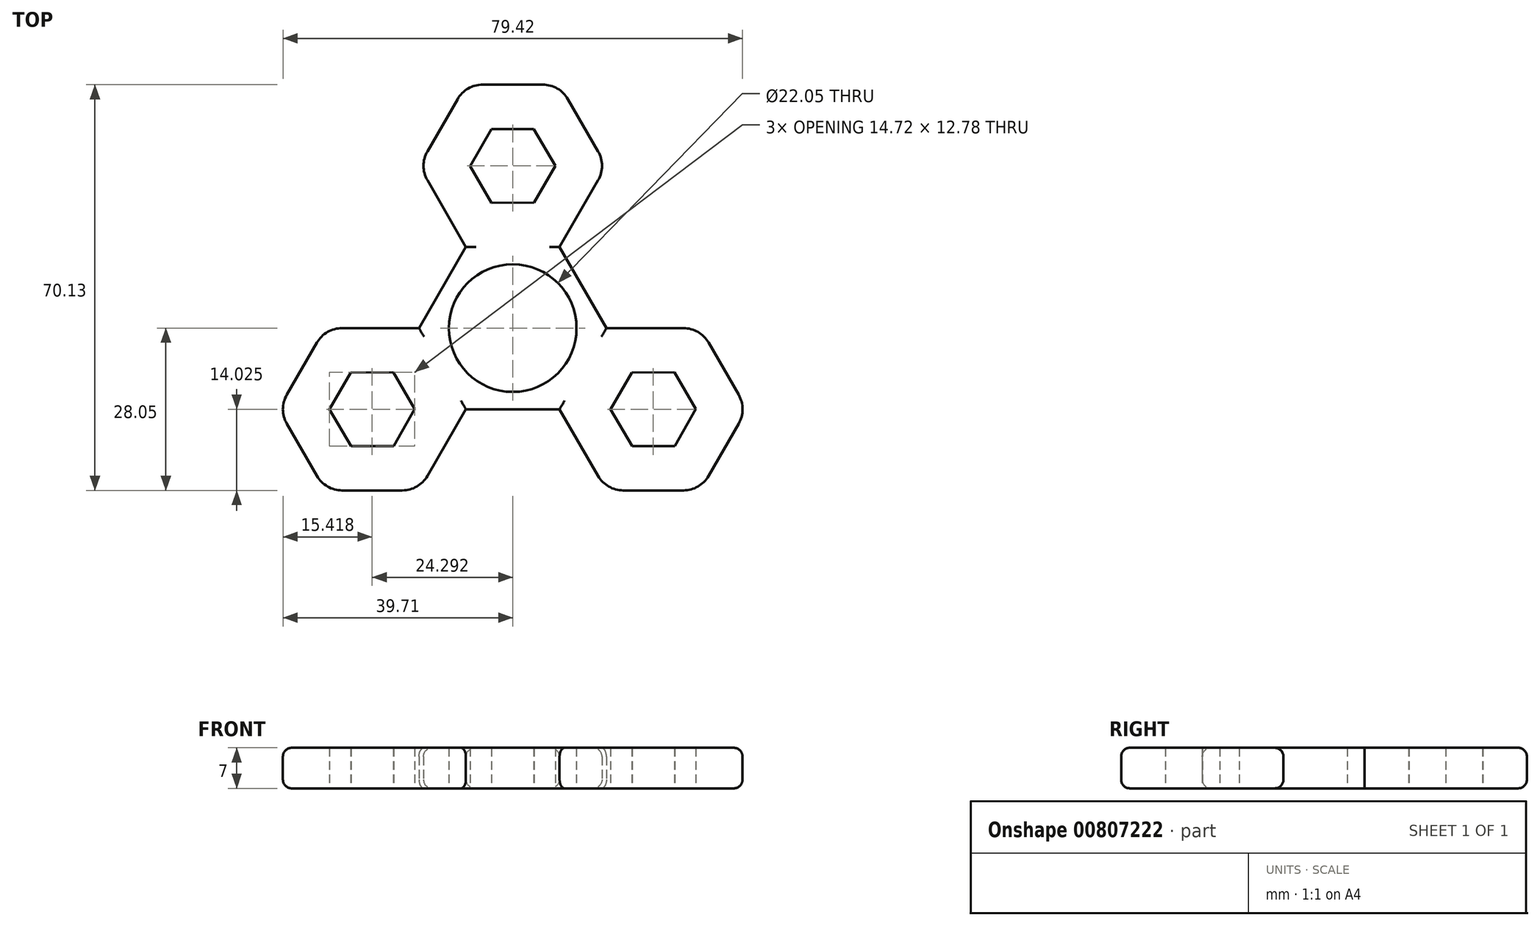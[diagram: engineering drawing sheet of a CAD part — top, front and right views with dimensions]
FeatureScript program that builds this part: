
annotation { "Feature Type Name" : "Feature", "Feature Type Description" : "" }
export const myFeature = defineFeature(function(context is Context, id is Id, definition is map)
    precondition{}
    {
        {
            var Q0;
            Q0=qCreatedBy(makeId("Top.planeOp"),FACE);
            var sketch = newSketch(context, id + "F0", { "sketchPlane" : qUnion([Q0])});
            skCircle(sketch, "E0", {"center": v(0, 0) * mm, "radius": 11.03 * mm});
            skCircle(sketch, "E1.cCircle", {"center": v(0, 0) * mm, "radius": 14.03 * mm, "construction": true});
            skLineSegment(sketch, "E1.1", {"start": v(8.1, -14.02) * mm, "end": v(-8.1, -14.03) * mm});
            skLineSegment(sketch, "E1.3", {"start": v(-16.2, 0) * mm, "end": v(-8.1, 14.03) * mm});
            skLineSegment(sketch, "E1.5", {"start": v(8.1, 14.02) * mm, "end": v(16.2, 0) * mm});
            skPoint(sketch, "E1.0.midPoint", {"position": v(12.15, -7.01) * mm});
            skCircle(sketch, "E2.cCircle", {"center": v(0, 28.05) * mm, "radius": 6.38 * mm, "construction": true});
            skLineSegment(sketch, "E2.0", {"start": v(7.36, 28.08) * mm, "end": v(3.7, 21.69) * mm});
            skLineSegment(sketch, "E2.1", {"start": v(3.7, 21.69) * mm, "end": v(-3.66, 21.66) * mm});
            skLineSegment(sketch, "E2.2", {"start": v(-3.66, 21.66) * mm, "end": v(-7.36, 28.02) * mm});
            skLineSegment(sketch, "E2.3", {"start": v(-7.36, 28.02) * mm, "end": v(-3.7, 34.41) * mm});
            skLineSegment(sketch, "E2.4", {"start": v(-3.7, 34.41) * mm, "end": v(3.66, 34.44) * mm});
            skLineSegment(sketch, "E2.5", {"start": v(3.66, 34.44) * mm, "end": v(7.36, 28.08) * mm});
            skPoint(sketch, "E2.0.midPoint", {"position": v(5.53, 24.88) * mm});
            skCircle(sketch, "E3.cCircle", {"center": v(0, 28.05) * mm, "radius": 14.03 * mm, "construction": true});
            skLineSegment(sketch, "E3.0", {"start": v(16.2, 28.05) * mm, "end": v(8.1, 14.02) * mm});
            skLineSegment(sketch, "E3.2", {"start": v(-8.1, 14.02) * mm, "end": v(-16.2, 28.05) * mm});
            skLineSegment(sketch, "E3.3", {"start": v(-16.2, 28.05) * mm, "end": v(-8.1, 42.07) * mm});
            skLineSegment(sketch, "E3.4", {"start": v(-8.1, 42.07) * mm, "end": v(8.1, 42.07) * mm});
            skLineSegment(sketch, "E3.5", {"start": v(8.1, 42.07) * mm, "end": v(16.2, 28.05) * mm});
            skPoint(sketch, "E3.0.midPoint", {"position": v(12.15, 21.04) * mm});
            skLineSegment(sketch, "E4.1.6", {"start": v(-16.2, -28.05) * mm, "end": v(-32.39, -28.05) * mm});
            skLineSegment(sketch, "E4.1.7", {"start": v(-32.39, -28.05) * mm, "end": v(-40.49, -14.02) * mm});
            skLineSegment(sketch, "E4.1.8", {"start": v(-40.49, -14.02) * mm, "end": v(-32.39, 0) * mm});
            skLineSegment(sketch, "E4.1.9", {"start": v(-32.39, 0) * mm, "end": v(-16.2, 0) * mm});
            skLineSegment(sketch, "E4.1.10", {"start": v(-8.1, -14.02) * mm, "end": v(-16.2, -28.05) * mm});
            skLineSegment(sketch, "E4.2.6", {"start": v(32.39, 0) * mm, "end": v(40.49, -14.02) * mm});
            skLineSegment(sketch, "E4.2.7", {"start": v(40.49, -14.02) * mm, "end": v(32.39, -28.05) * mm});
            skLineSegment(sketch, "E4.2.8", {"start": v(32.39, -28.05) * mm, "end": v(16.2, -28.05) * mm});
            skLineSegment(sketch, "E4.2.9", {"start": v(16.2, -28.05) * mm, "end": v(8.1, -14.02) * mm});
            skLineSegment(sketch, "E4.2.10", {"start": v(16.2, 0) * mm, "end": v(32.39, 0) * mm});
            skLineSegment(sketch, "E5.1.0", {"start": v(-27.95, -20.41) * mm, "end": v(-31.65, -14.05) * mm});
            skLineSegment(sketch, "E5.1.1", {"start": v(-31.65, -14.05) * mm, "end": v(-28, -7.66) * mm});
            skLineSegment(sketch, "E5.1.2", {"start": v(-28, -7.66) * mm, "end": v(-20.63, -7.64) * mm});
            skLineSegment(sketch, "E5.1.3", {"start": v(-20.63, -7.64) * mm, "end": v(-16.93, -14) * mm});
            skLineSegment(sketch, "E5.1.4", {"start": v(-16.93, -14) * mm, "end": v(-20.59, -20.39) * mm});
            skLineSegment(sketch, "E5.1.5", {"start": v(-20.59, -20.39) * mm, "end": v(-27.95, -20.41) * mm});
            skLineSegment(sketch, "E5.2.0", {"start": v(31.65, -14) * mm, "end": v(28, -20.39) * mm});
            skLineSegment(sketch, "E5.2.1", {"start": v(28, -20.39) * mm, "end": v(20.63, -20.41) * mm});
            skLineSegment(sketch, "E5.2.2", {"start": v(20.63, -20.41) * mm, "end": v(16.93, -14.05) * mm});
            skLineSegment(sketch, "E5.2.3", {"start": v(16.93, -14.05) * mm, "end": v(20.59, -7.66) * mm});
            skLineSegment(sketch, "E5.2.4", {"start": v(20.59, -7.66) * mm, "end": v(27.95, -7.64) * mm});
            skLineSegment(sketch, "E5.2.5", {"start": v(27.95, -7.64) * mm, "end": v(31.65, -14) * mm});
            skSolve(sketch);
        }
        {
            var Q0;
            Q0=makeQuery(id+"F0.imprint","IMPRINT",FACE,{"disambiguationData":[TD([[makeQuery(id+"F0.imprint","IMPRINT",EDGE,{"derivedFrom":sQuery(id+"F0.wireOp",EDGE,"E0")}),-1.0]])]});
            extrude(context, id + "F1", {"entities" : qUnion([Q0]), "depth" : 7 * mm, "offsetDistance" : 25 * mm});
        }
        {
            var Q0;
            Q0=makeQuery(id+"F1.opExtrude","CAP_EDGE",EDGE,{"disambiguationData":[OSD([sQuery(id+"F0.wireOp",EDGE,"E4.1.10")])],"isStart":false});
            var Q1;
            Q1=makeQuery(id+"F1.opExtrude","CAP_EDGE",EDGE,{"disambiguationData":[OSD([sQuery(id+"F0.wireOp",EDGE,"E4.1.6")])],"isStart":false});
            var Q2;
            Q2=makeQuery(id+"F1.opExtrude","CAP_EDGE",EDGE,{"disambiguationData":[OSD([sQuery(id+"F0.wireOp",EDGE,"E4.1.7")])],"isStart":false});
            var Q3;
            Q3=makeQuery(id+"F1.opExtrude","CAP_EDGE",EDGE,{"disambiguationData":[OSD([sQuery(id+"F0.wireOp",EDGE,"E4.1.8")])],"isStart":false});
            var Q4;
            Q4=makeQuery(id+"F1.opExtrude","CAP_EDGE",EDGE,{"disambiguationData":[OSD([sQuery(id+"F0.wireOp",EDGE,"E4.1.9")])],"isStart":false});
            var Q5;
            Q5=makeQuery(id+"F1.opExtrude","CAP_EDGE",EDGE,{"disambiguationData":[OSD([sQuery(id+"F0.wireOp",EDGE,"E1.3")])],"isStart":false});
            var Q6;
            Q6=makeQuery(id+"F1.opExtrude","CAP_EDGE",EDGE,{"disambiguationData":[OSD([sQuery(id+"F0.wireOp",EDGE,"E3.2")])],"isStart":false});
            var Q7;
            Q7=makeQuery(id+"F1.opExtrude","CAP_EDGE",EDGE,{"disambiguationData":[OSD([sQuery(id+"F0.wireOp",EDGE,"E3.3")])],"isStart":false});
            var Q8;
            Q8=makeQuery(id+"F1.opExtrude","CAP_EDGE",EDGE,{"disambiguationData":[OSD([sQuery(id+"F0.wireOp",EDGE,"E3.4")])],"isStart":false});
            var Q9;
            Q9=makeQuery(id+"F1.opExtrude","CAP_EDGE",EDGE,{"disambiguationData":[OSD([sQuery(id+"F0.wireOp",EDGE,"E3.5")])],"isStart":false});
            var Q10;
            Q10=makeQuery(id+"F1.opExtrude","CAP_EDGE",EDGE,{"disambiguationData":[OSD([sQuery(id+"F0.wireOp",EDGE,"E3.0")])],"isStart":false});
            var Q11;
            Q11=makeQuery(id+"F1.opExtrude","CAP_EDGE",EDGE,{"disambiguationData":[OSD([sQuery(id+"F0.wireOp",EDGE,"E1.5")])],"isStart":false});
            var Q12;
            Q12=makeQuery(id+"F1.opExtrude","CAP_EDGE",EDGE,{"disambiguationData":[OSD([sQuery(id+"F0.wireOp",EDGE,"E4.2.10")])],"isStart":false});
            var Q13;
            Q13=makeQuery(id+"F1.opExtrude","CAP_EDGE",EDGE,{"disambiguationData":[OSD([sQuery(id+"F0.wireOp",EDGE,"E4.2.6")])],"isStart":false});
            var Q14;
            Q14=makeQuery(id+"F1.opExtrude","CAP_EDGE",EDGE,{"disambiguationData":[OSD([sQuery(id+"F0.wireOp",EDGE,"E4.2.7")])],"isStart":false});
            var Q15;
            Q15=makeQuery(id+"F1.opExtrude","CAP_EDGE",EDGE,{"disambiguationData":[OSD([sQuery(id+"F0.wireOp",EDGE,"E4.2.8")])],"isStart":false});
            var Q16;
            Q16=makeQuery(id+"F1.opExtrude","CAP_EDGE",EDGE,{"disambiguationData":[OSD([sQuery(id+"F0.wireOp",EDGE,"E4.2.9")])],"isStart":false});
            var Q17;
            Q17=makeQuery(id+"F1.opExtrude","CAP_EDGE",EDGE,{"disambiguationData":[OSD([sQuery(id+"F0.wireOp",EDGE,"E1.1")])],"isStart":false});
            var Q18;
            Q18=makeQuery(id+"F1.opExtrude","CAP_EDGE",EDGE,{"disambiguationData":[OSD([sQuery(id+"F0.wireOp",EDGE,"E1.1")])],"isStart":true});
            var Q19;
            Q19=makeQuery(id+"F1.opExtrude","CAP_EDGE",EDGE,{"disambiguationData":[OSD([sQuery(id+"F0.wireOp",EDGE,"E4.1.10")])],"isStart":true});
            var Q20;
            Q20=makeQuery(id+"F1.opExtrude","CAP_EDGE",EDGE,{"disambiguationData":[OSD([sQuery(id+"F0.wireOp",EDGE,"E4.1.6")])],"isStart":true});
            var Q21;
            Q21=makeQuery(id+"F1.opExtrude","CAP_EDGE",EDGE,{"disambiguationData":[OSD([sQuery(id+"F0.wireOp",EDGE,"E4.1.7")])],"isStart":true});
            var Q22;
            Q22=makeQuery(id+"F1.opExtrude","CAP_EDGE",EDGE,{"disambiguationData":[OSD([sQuery(id+"F0.wireOp",EDGE,"E4.1.8")])],"isStart":true});
            var Q23;
            Q23=makeQuery(id+"F1.opExtrude","CAP_EDGE",EDGE,{"disambiguationData":[OSD([sQuery(id+"F0.wireOp",EDGE,"E4.1.9")])],"isStart":true});
            var Q24;
            Q24=makeQuery(id+"F1.opExtrude","CAP_EDGE",EDGE,{"disambiguationData":[OSD([sQuery(id+"F0.wireOp",EDGE,"E1.3")])],"isStart":true});
            var Q25;
            Q25=makeQuery(id+"F1.opExtrude","CAP_EDGE",EDGE,{"disambiguationData":[OSD([sQuery(id+"F0.wireOp",EDGE,"E4.2.9")])],"isStart":true});
            var Q26;
            Q26=makeQuery(id+"F1.opExtrude","CAP_EDGE",EDGE,{"disambiguationData":[OSD([sQuery(id+"F0.wireOp",EDGE,"E4.2.8")])],"isStart":true});
            var Q27;
            Q27=makeQuery(id+"F1.opExtrude","CAP_EDGE",EDGE,{"disambiguationData":[OSD([sQuery(id+"F0.wireOp",EDGE,"E4.2.7")])],"isStart":true});
            var Q28;
            Q28=makeQuery(id+"F1.opExtrude","CAP_EDGE",EDGE,{"disambiguationData":[OSD([sQuery(id+"F0.wireOp",EDGE,"E4.2.6")])],"isStart":true});
            var Q29;
            Q29=makeQuery(id+"F1.opExtrude","CAP_EDGE",EDGE,{"disambiguationData":[OSD([sQuery(id+"F0.wireOp",EDGE,"E4.2.10")])],"isStart":true});
            var Q30;
            Q30=makeQuery(id+"F1.opExtrude","CAP_EDGE",EDGE,{"disambiguationData":[OSD([sQuery(id+"F0.wireOp",EDGE,"E1.5")])],"isStart":true});
            var Q31;
            Q31=makeQuery(id+"F1.opExtrude","CAP_EDGE",EDGE,{"disambiguationData":[OSD([sQuery(id+"F0.wireOp",EDGE,"E3.0")])],"isStart":true});
            var Q32;
            Q32=makeQuery(id+"F1.opExtrude","CAP_EDGE",EDGE,{"disambiguationData":[OSD([sQuery(id+"F0.wireOp",EDGE,"E3.5")])],"isStart":true});
            var Q33;
            Q33=makeQuery(id+"F1.opExtrude","CAP_EDGE",EDGE,{"disambiguationData":[OSD([sQuery(id+"F0.wireOp",EDGE,"E3.4")])],"isStart":true});
            var Q34;
            Q34=makeQuery(id+"F1.opExtrude","CAP_EDGE",EDGE,{"disambiguationData":[OSD([sQuery(id+"F0.wireOp",EDGE,"E3.3")])],"isStart":true});
            var Q35;
            Q35=makeQuery(id+"F1.opExtrude","CAP_EDGE",EDGE,{"disambiguationData":[OSD([sQuery(id+"F0.wireOp",EDGE,"E3.2")])],"isStart":true});
            fillet(context, id + "F2", {"entities" : qUnion([Q0, Q1, Q2, Q3, Q4, Q5, Q6, Q7, Q8, Q9, Q10, Q11, Q12, Q13, Q14, Q15, Q16, Q17, Q18, Q19, Q20, Q21, Q22, Q23, Q24, Q25, Q26, Q27, Q28, Q29, Q30, Q31, Q32, Q33, Q34, Q35]), "radius" : 1.5 * mm, "tangentPropagation" : true, "allowEdgeOverflow" : false});
        }
        {
            var Q0;
            Q0=makeQuery(id+"F1.opExtrude","SWEPT_EDGE",EDGE,{"disambiguationData":[OSD([sQuery(id+"F0.wireOp",EDGE,"E4.1.6"),sQuery(id+"F0.wireOp",EDGE,"E4.1.10")])]});
            var Q1;
            Q1=makeQuery(id+"F1.opExtrude","SWEPT_EDGE",EDGE,{"disambiguationData":[OSD([sQuery(id+"F0.wireOp",EDGE,"E4.1.6"),sQuery(id+"F0.wireOp",EDGE,"E4.1.7")])]});
            var Q2;
            Q2=makeQuery(id+"F1.opExtrude","SWEPT_EDGE",EDGE,{"disambiguationData":[OSD([sQuery(id+"F0.wireOp",EDGE,"E4.1.7"),sQuery(id+"F0.wireOp",EDGE,"E4.1.8")])]});
            var Q3;
            Q3=makeQuery(id+"F1.opExtrude","SWEPT_EDGE",EDGE,{"disambiguationData":[OSD([sQuery(id+"F0.wireOp",EDGE,"E4.1.8"),sQuery(id+"F0.wireOp",EDGE,"E4.1.9")])]});
            var Q4;
            Q4=makeQuery(id+"F1.opExtrude","SWEPT_EDGE",EDGE,{"disambiguationData":[OSD([sQuery(id+"F0.wireOp",EDGE,"E3.2"),sQuery(id+"F0.wireOp",EDGE,"E3.3")])]});
            var Q5;
            Q5=makeQuery(id+"F1.opExtrude","SWEPT_EDGE",EDGE,{"disambiguationData":[OSD([sQuery(id+"F0.wireOp",EDGE,"E3.3"),sQuery(id+"F0.wireOp",EDGE,"E3.4")])]});
            var Q6;
            Q6=makeQuery(id+"F1.opExtrude","SWEPT_EDGE",EDGE,{"disambiguationData":[OSD([sQuery(id+"F0.wireOp",EDGE,"E3.4"),sQuery(id+"F0.wireOp",EDGE,"E3.5")])]});
            var Q7;
            Q7=makeQuery(id+"F1.opExtrude","SWEPT_EDGE",EDGE,{"disambiguationData":[OSD([sQuery(id+"F0.wireOp",EDGE,"E3.0"),sQuery(id+"F0.wireOp",EDGE,"E3.5")])]});
            var Q8;
            Q8=makeQuery(id+"F1.opExtrude","SWEPT_EDGE",EDGE,{"disambiguationData":[OSD([sQuery(id+"F0.wireOp",EDGE,"E4.2.6"),sQuery(id+"F0.wireOp",EDGE,"E4.2.10")])]});
            var Q9;
            Q9=makeQuery(id+"F1.opExtrude","SWEPT_EDGE",EDGE,{"disambiguationData":[OSD([sQuery(id+"F0.wireOp",EDGE,"E4.2.6"),sQuery(id+"F0.wireOp",EDGE,"E4.2.7")])]});
            var Q10;
            Q10=makeQuery(id+"F1.opExtrude","SWEPT_EDGE",EDGE,{"disambiguationData":[OSD([sQuery(id+"F0.wireOp",EDGE,"E4.2.7"),sQuery(id+"F0.wireOp",EDGE,"E4.2.8")])]});
            var Q11;
            Q11=makeQuery(id+"F1.opExtrude","SWEPT_EDGE",EDGE,{"disambiguationData":[OSD([sQuery(id+"F0.wireOp",EDGE,"E4.2.8"),sQuery(id+"F0.wireOp",EDGE,"E4.2.9")])]});
            fillet(context, id + "F3", {"entities" : qUnion([Q0, Q1, Q2, Q3, Q4, Q5, Q6, Q7, Q8, Q9, Q10, Q11]), "radius" : 5 * mm, "tangentPropagation" : true, "allowEdgeOverflow" : false});
        }
    });
